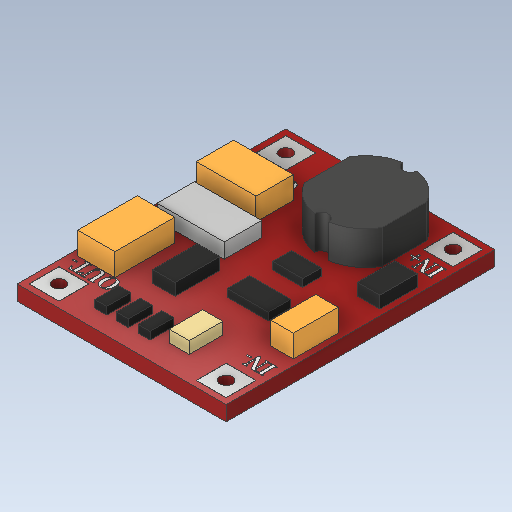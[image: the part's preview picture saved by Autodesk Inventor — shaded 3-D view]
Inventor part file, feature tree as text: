
AUTODESK INVENTOR PART (.ipt)
format: ipt  version: 2020.1 (Build 241239000, 239)  size: 973,824 bytes
history: native  units: mm
features: extrude x7, sketch x2, emboss x1, other x1
ambient origin geometry x8: Origin, YZ Plane, XZ Plane, XY Plane, X Axis, Y Axis, Z Axis, Center Point
bodies: Solid1 (feature_tree)
feature tree (11):
  sketch  "Sketch1"  dims[d0=14.0mm d1=18.0mm]
  extrude  "Extrusion1"  Depth=18.0mm
  extrude  "Extrusion2"  Depth=0.01mm
  extrude  "Extrusion3"  Depth=0.01mm
  extrude  "Extrusion4"  Depth=0.01mm
  extrude  "Extrusion5"  Depth=0.01mm
  extrude  "Extrusion6"  Depth=0.01mm
  extrude  "Extrusion7"  Depth=0.01mm
  emboss  "Emboss1"
  other  "Image1"
  sketch  "Sketch2"  dims[d26=2.0mm d33=0.4mm d34=0.4mm d35=0.4mm d36=0.4mm d37=0.4mm d38=0.4mm d39=0.4mm d44=0.4mm d45=0.85mm d47=1.0mm d50=1.0mm d51=1.0mm d52=1.0mm d59=2.5mm d60=4.0mm d62=0.4mm d63=1.25mm d64=4.0mm d65=2.5mm d67=0.4mm d68=1.5mm d69=6.0mm d71=0.5mm d72=0.5mm d74=3.0mm d76=3.25mm d77=3.0mm d78=3.0mm d80=3.0mm d83=1.5mm d84=3.0mm d85=0.4mm d86=2.5mm d87=4.5mm d88=2.5mm d89=1.0mm d90=2.0mm d91=1.25mm d95=2.25mm d96=1.0mm d97=2.75mm d98=1.5mm d100=1.6mm d101=2.3mm d102=1.5mm d103=2.5mm d104=0.4mm d105=2.8mm d106=1.35mm d107=2.25mm d110=2.35mm d111=1.75mm d112=1.6mm d113=0.8mm d114=0.8mm d115=1.2mm d117=0.65mm d118=0.65mm d119=1.5mm d120=3.0mm d122=0.8mm d123=1.6mm d124=1.0mm d125=0.0mm d126=0.01mm d127=0.0mm d128=1.5mm d129=0.0mm d130=1.0mm d131=0.0mm d132=0.8mm d133=0.0mm d134=0.5mm d135=0.0mm d136=2.25mm d137=0.0mm d138=0.5mm d139=0.5mm d140=0.2mm d141=0.01mm d142=0.0mm]
